# Revit family: revitupgrade
name_source: partatom
category: Furniture
units: mm (PartAtom-declared; Revit-internal decimal feet)

## family parameters
Always vertical = Yes
Cut with Voids When Loaded = No
Enable Cutting in Views = No
OmniClass Number = 23.40.70.14.64.11
OmniClass Title = Office Furniture
Render Appearance Source = Family Geometry
Room Calculation Point = No
Shared = No
Work Plane-Based = No

## types (1)
- 14"
    Assembly Code = E2020200
    Casters = SmithSystem_Plastic_Black
    Default Elevation = 0.00"
    Description = Numbers™ chair and desk were created to address a conceptual need that emerged from early design charettes: a value driven affordable K12 chair and desk meeting specifications all over the world, providing unparalleled performance and visual subtlety.
    Frame Finish = SmithSystem_Metal_Platinum
    Manufacturer = Smith System
    Release Date = August 2023
    Style Number(s) = 22860
    URL = https://www.steelcase.com

## geometry (parser evidence)
native form markers: Sweep x2
no freeform markers — native parametric forms only
